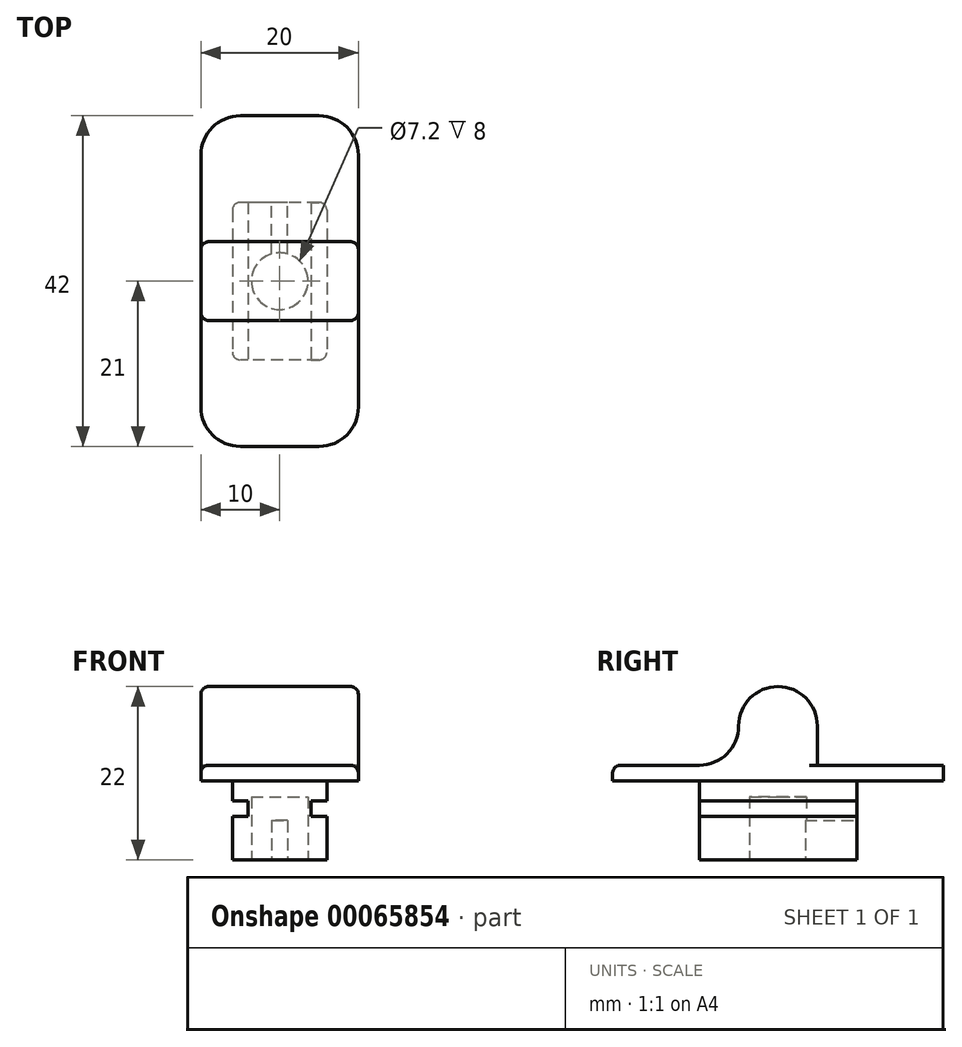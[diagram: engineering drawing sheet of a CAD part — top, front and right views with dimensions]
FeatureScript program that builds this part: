
annotation { "Feature Type Name" : "Feature", "Feature Type Description" : "" }
export const myFeature = defineFeature(function(context is Context, id is Id, definition is map)
    precondition{}
    {
        {
            var Q0;
            Q0=qCreatedBy(makeId("Top.planeOp"),FACE);
            var sketch = newSketch(context, id + "F0", { "sketchPlane" : qUnion([Q0])});
            skLineSegment(sketch, "E0.bottom", {"start": v(10, -21) * mm, "end": v(-10, -21) * mm});
            skLineSegment(sketch, "E0.top", {"start": v(10, 21) * mm, "end": v(-10, 21) * mm});
            skLineSegment(sketch, "E0.left", {"start": v(10, -21) * mm, "end": v(10, 21) * mm});
            skLineSegment(sketch, "E0.right", {"start": v(-10, -21) * mm, "end": v(-10, 21) * mm});
            skPoint(sketch, "E0.middle", {"position": v(0, 0) * mm});
            skSolve(sketch);
        }
        {
            var Q0;
            Q0 = qSketchRegion(id + "F0", true);
            extrude(context, id + "F1", {"entities" : qUnion([Q0]), "depth" : 2 * mm});
        }
        {
            var Q0;
            Q0=qCreatedBy(makeId("Top.planeOp"),FACE);
            var sketch = newSketch(context, id + "F2", { "sketchPlane" : qUnion([Q0])});
            skLineSegment(sketch, "E1.bottom", {"start": v(6, 10) * mm, "end": v(-6, 10) * mm});
            skLineSegment(sketch, "E1.top", {"start": v(6, -10) * mm, "end": v(-6, -10) * mm});
            skLineSegment(sketch, "E1.left", {"start": v(6, 10) * mm, "end": v(6, -10) * mm});
            skLineSegment(sketch, "E1.right", {"start": v(-6, 10) * mm, "end": v(-6, -10) * mm});
            skPoint(sketch, "E1.middle", {"position": v(0, 0) * mm});
            skSolve(sketch);
        }
        {
            var Q0;
            Q0 = qSketchRegion(id + "F2", true);
            extrude(context, id + "F3", {"entities" : qUnion([Q0]), "operationType" : NewBodyOperationType.ADD, "oppositeDirection" : true, "depth" : 10 * mm});
        }
        {
            var Q0;
            Q0=makeQuery(id+"F3.opExtrude","SWEPT_EDGE",EDGE,{"disambiguationData":[OSD([sQuery(id+"F2.wireOp",EDGE,"E1.top"),sQuery(id+"F2.wireOp",EDGE,"E1.right")])]});
            var Q1;
            Q1=makeQuery(id+"F3.opExtrude","SWEPT_EDGE",EDGE,{"disambiguationData":[OSD([sQuery(id+"F2.wireOp",EDGE,"E1.top"),sQuery(id+"F2.wireOp",EDGE,"E1.left")])]});
            var Q2;
            Q2=makeQuery(id+"F3.opExtrude","SWEPT_EDGE",EDGE,{"disambiguationData":[OSD([sQuery(id+"F2.wireOp",EDGE,"E1.bottom"),sQuery(id+"F2.wireOp",EDGE,"E1.right")])]});
            var Q3;
            Q3=makeQuery(id+"F3.opExtrude","SWEPT_EDGE",EDGE,{"disambiguationData":[OSD([sQuery(id+"F2.wireOp",EDGE,"E1.bottom"),sQuery(id+"F2.wireOp",EDGE,"E1.left")])]});
            fillet(context, id + "F4", {"entities" : qUnion([Q0, Q1, Q2, Q3]), "radius" : 1 * mm, "tangentPropagation" : true, "allowEdgeOverflow" : false});
        }
        {
            var Q0;
            Q0=makeQuery(id+"F1.opExtrude","CAP_FACE",FACE,{"disambiguationData":[OSD([sQuery(id+"F0.wireOp",EDGE,"E0.bottom"),sQuery(id+"F0.wireOp",EDGE,"E0.top"),sQuery(id+"F0.wireOp",EDGE,"E0.left"),sQuery(id+"F0.wireOp",EDGE,"E0.right")])],"isStart":false});
            var sketch = newSketch(context, id + "F5", { "sketchPlane" : qUnion([Q0])});
            skLineSegment(sketch, "E2.bottom", {"start": v(10, -5) * mm, "end": v(-10, -5) * mm});
            skLineSegment(sketch, "E2.top", {"start": v(10, 5) * mm, "end": v(-10, 5) * mm});
            skLineSegment(sketch, "E2.left", {"start": v(10, -5) * mm, "end": v(10, 5) * mm});
            skLineSegment(sketch, "E2.right", {"start": v(-10, -5) * mm, "end": v(-10, 5) * mm});
            skPoint(sketch, "E2.middle", {"position": v(0, 0) * mm});
            skSolve(sketch);
        }
        {
            var Q0;
            Q0 = qSketchRegion(id + "F5", true);
            extrude(context, id + "F6", {"entities" : qUnion([Q0]), "operationType" : NewBodyOperationType.ADD, "depth" : 10 * mm});
        }
        {
            var Q0;
            Q0=makeQuery(id+"F6.opExtrude","CAP_EDGE",EDGE,{"disambiguationData":[OSD([sQuery(id+"F5.wireOp",EDGE,"E2.bottom")])],"isStart":false});
            var Q1;
            Q1=makeQuery(id+"F6.opExtrude","CAP_EDGE",EDGE,{"disambiguationData":[OSD([sQuery(id+"F5.wireOp",EDGE,"E2.top")])],"isStart":false});
            var Q2;
            Q2=makeQuery(id+"F6.opExtrude","CAP_EDGE",EDGE,{"disambiguationData":[OSD([sQuery(id+"F5.wireOp",EDGE,"E2.bottom")])],"isStart":true});
            var Q3;
            Q3=makeQuery(id+"F6.opExtrude","CAP_EDGE",EDGE,{"disambiguationData":[OSD([sQuery(id+"F5.wireOp",EDGE,"E2.top")])],"isStart":true});
            fillet(context, id + "F7", {"entities" : qUnion([Q0, Q1, Q2, Q3]), "radius" : 5 * mm, "tangentPropagation" : true, "allowEdgeOverflow" : false});
        }
        {
            var Q0;
            Q0=makeQuery(id+"F3.opExtrude","CAP_FACE",FACE,{"disambiguationData":[OSD([sQuery(id+"F2.wireOp",EDGE,"E1.bottom"),sQuery(id+"F2.wireOp",EDGE,"E1.top"),sQuery(id+"F2.wireOp",EDGE,"E1.left"),sQuery(id+"F2.wireOp",EDGE,"E1.right")])],"isStart":false});
            var sketch = newSketch(context, id + "F8", { "sketchPlane" : qUnion([Q0])});
            skCircle(sketch, "E3", {"center": v(0, 0) * mm, "radius": 3.6 * mm});
            skSolve(sketch);
        }
        {
            var Q0;
            Q0 = qSketchRegion(id + "F8", true);
            extrude(context, id + "F9", {"entities" : qUnion([Q0]), "operationType" : NewBodyOperationType.REMOVE, "oppositeDirection" : true, "depth" : 8 * mm});
        }
        {
            var Q0;
            Q0=makeQuery(id+"F3.opExtrude","SWEPT_FACE",FACE,{"disambiguationData":[OSD([sQuery(id+"F2.wireOp",EDGE,"E1.bottom")])]});
            var sketch = newSketch(context, id + "F10", { "sketchPlane" : qUnion([Q0])});
            skLineSegment(sketch, "E4.bottom", {"start": v(-1, -5) * mm, "end": v(1, -5) * mm});
            skLineSegment(sketch, "E4.top", {"start": v(-1, -15) * mm, "end": v(1, -15) * mm});
            skLineSegment(sketch, "E4.left", {"start": v(-1, -5) * mm, "end": v(-1, -15) * mm});
            skLineSegment(sketch, "E4.right", {"start": v(1, -5) * mm, "end": v(1, -15) * mm});
            skPoint(sketch, "E4.middle", {"position": v(0, -10) * mm});
            skSolve(sketch);
        }
        {
            var Q0;
            {var subQ0=sQuery(id+"F10.wireOp",EDGE,"E4.bottom");Q0=makeQuery(id+"F10.imprint","IMPRINT",FACE,{"disambiguationData":[TD([[makeQuery(id+"F10.imprint","IMPRINT",EDGE,{"derivedFrom":subQ0}),-1.0]])]});}
            extrude(context, id + "F11", {"entities" : qUnion([Q0]), "operationType" : NewBodyOperationType.REMOVE, "oppositeDirection" : true, "depth" : 7 * mm});
        }
        {
            var Q0;
            Q0=makeQuery(id+"F1.opExtrude","SWEPT_EDGE",EDGE,{"disambiguationData":[OSD([sQuery(id+"F0.wireOp",EDGE,"E0.bottom"),sQuery(id+"F0.wireOp",EDGE,"E0.left")])]});
            var Q1;
            Q1=makeQuery(id+"F1.opExtrude","SWEPT_EDGE",EDGE,{"disambiguationData":[OSD([sQuery(id+"F0.wireOp",EDGE,"E0.top"),sQuery(id+"F0.wireOp",EDGE,"E0.right")])]});
            var Q2;
            Q2=makeQuery(id+"F1.opExtrude","SWEPT_EDGE",EDGE,{"disambiguationData":[OSD([sQuery(id+"F0.wireOp",EDGE,"E0.top"),sQuery(id+"F0.wireOp",EDGE,"E0.left")])]});
            var Q3;
            Q3=makeQuery(id+"F1.opExtrude","SWEPT_EDGE",EDGE,{"disambiguationData":[OSD([sQuery(id+"F0.wireOp",EDGE,"E0.bottom"),sQuery(id+"F0.wireOp",EDGE,"E0.right")])]});
            fillet(context, id + "F12", {"entities" : qUnion([Q0, Q1, Q2, Q3]), "radius" : 5 * mm, "tangentPropagation" : true, "allowEdgeOverflow" : false});
        }
        {
            var Q0;
            Q0=makeQuery(id+"F3.opExtrude","SWEPT_FACE",FACE,{"disambiguationData":[OSD([sQuery(id+"F2.wireOp",EDGE,"E1.right")])]});
            var sketch = newSketch(context, id + "F13", { "sketchPlane" : qUnion([Q0])});
            skLineSegment(sketch, "E5.bottom", {"start": v(-13.45, -2.5) * mm, "end": v(11.55, -2.5) * mm});
            skLineSegment(sketch, "E5.top", {"start": v(-13.45, -4.5) * mm, "end": v(11.55, -4.5) * mm});
            skLineSegment(sketch, "E5.left", {"start": v(-13.45, -2.5) * mm, "end": v(-13.45, -4.5) * mm});
            skLineSegment(sketch, "E5.right", {"start": v(11.55, -2.5) * mm, "end": v(11.55, -4.5) * mm});
            skSolve(sketch);
        }
        {
            var Q0;
            Q0 = qSketchRegion(id + "F13", true);
            extrude(context, id + "F14", {"entities" : qUnion([Q0]), "operationType" : NewBodyOperationType.REMOVE, "oppositeDirection" : true, "depth" : 2 * mm});
        }
        {
            var Q0;
            Q0=makeQuery(id+"F3.opExtrude","SWEPT_FACE",FACE,{"disambiguationData":[OSD([sQuery(id+"F2.wireOp",EDGE,"E1.left")])]});
            var sketch = newSketch(context, id + "F15", { "sketchPlane" : qUnion([Q0])});
            skLineSegment(sketch, "E6.bottom", {"start": v(13.86, -4.5) * mm, "end": v(-14.44, -4.5) * mm});
            skLineSegment(sketch, "E6.top", {"start": v(13.86, -2.5) * mm, "end": v(-14.44, -2.5) * mm});
            skLineSegment(sketch, "E6.left", {"start": v(13.86, -4.5) * mm, "end": v(13.86, -2.5) * mm});
            skLineSegment(sketch, "E6.right", {"start": v(-14.44, -4.5) * mm, "end": v(-14.44, -2.5) * mm});
            skSolve(sketch);
        }
        {
            var Q0;
            Q0 = qSketchRegion(id + "F15", true);
            extrude(context, id + "F16", {"entities" : qUnion([Q0]), "operationType" : NewBodyOperationType.REMOVE, "oppositeDirection" : true, "depth" : 2 * mm});
        }
        {
            var Q0;
            Q0=makeQuery(id+"F7.opFillet","BLEND_EDGE",EDGE,{"blendedFrom":[makeQuery(id+"F6.opExtrude","CAP_EDGE",EDGE,{"disambiguationData":[OSD([sQuery(id+"F5.wireOp",EDGE,"E2.bottom")])],"isStart":false}),makeQuery(id+"F6.boolean.opBoolean","MERGE",FACE,{"derivedFrom":[makeQuery(id+"F1.opExtrude","SWEPT_FACE",FACE,{"disambiguationData":[OSD([sQuery(id+"F0.wireOp",EDGE,"E0.right")])]}),makeQuery(id+"F6.opExtrude","SWEPT_FACE",FACE,{"disambiguationData":[OSD([sQuery(id+"F5.wireOp",EDGE,"E2.right")])]})]})],"blendedInto":[makeQuery(id+"F6.boolean.opBoolean","MERGE",FACE,{"derivedFrom":[makeQuery(id+"F1.opExtrude","SWEPT_FACE",FACE,{"disambiguationData":[OSD([sQuery(id+"F0.wireOp",EDGE,"E0.right")])]}),makeQuery(id+"F6.opExtrude","SWEPT_FACE",FACE,{"disambiguationData":[OSD([sQuery(id+"F5.wireOp",EDGE,"E2.right")])]})]})]});
            fillet(context, id + "F17", {"entities" : qUnion([Q0]), "radius" : 1 * mm, "tangentPropagation" : true, "allowEdgeOverflow" : false});
        }
    });
